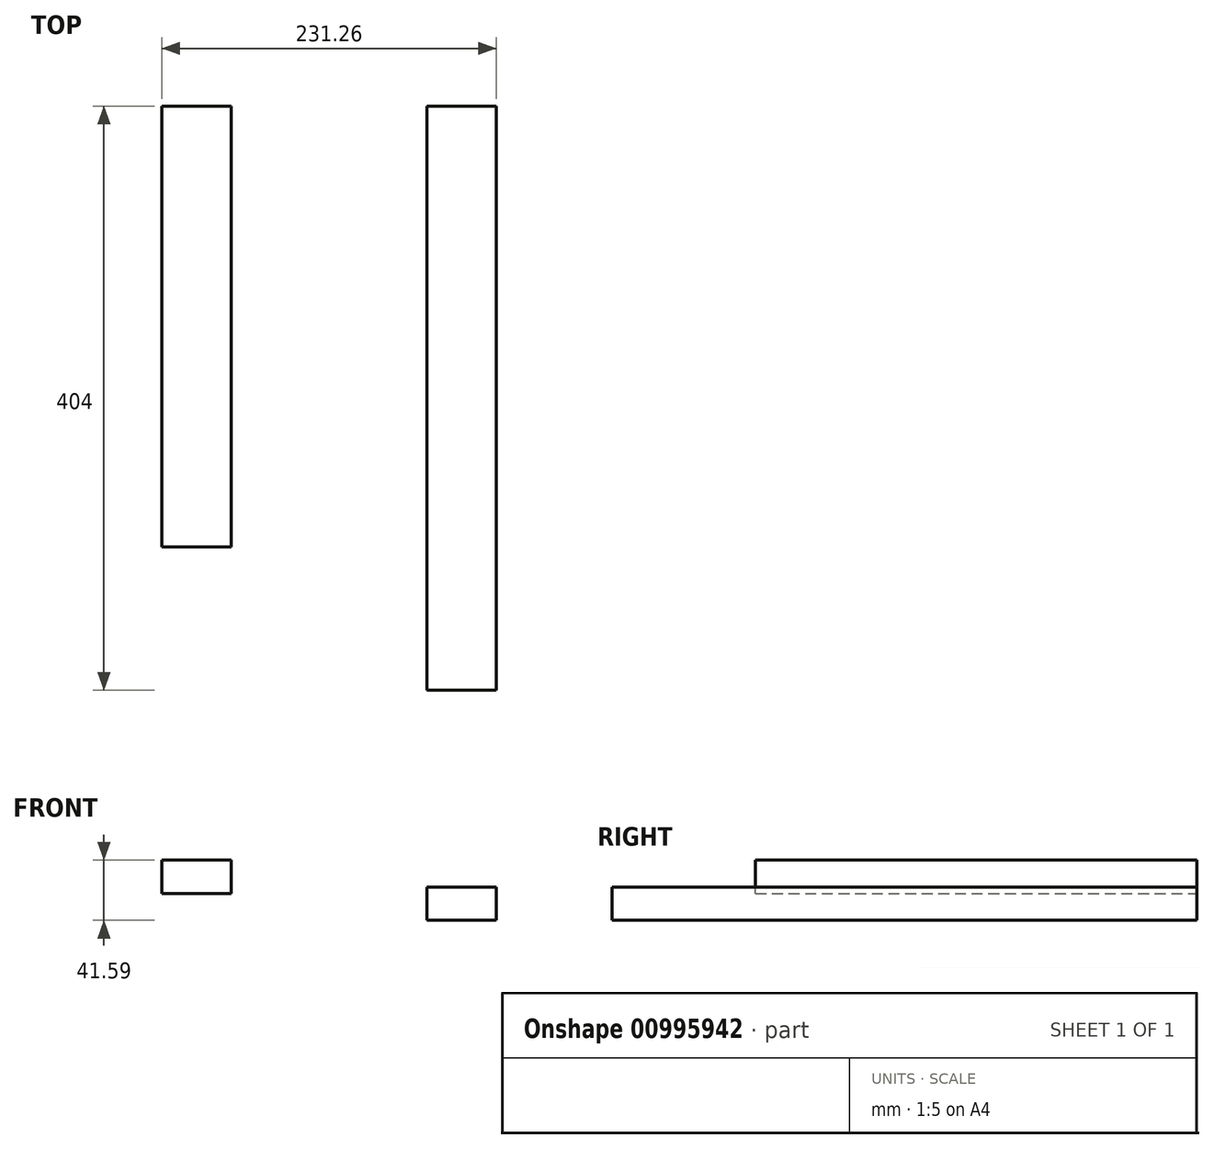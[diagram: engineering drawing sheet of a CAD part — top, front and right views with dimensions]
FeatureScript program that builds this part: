
annotation { "Feature Type Name" : "Feature", "Feature Type Description" : "" }
export const myFeature = defineFeature(function(context is Context, id is Id, definition is map)
    precondition{}
    {
        {
            assignVariable(context, id + "F0", {"name" : "Len", "anyValue" : 500 - 48 - 48});
        }
        {
            var Q0;
            Q0=qCreatedBy(makeId("Front.planeOp"),FACE);
            var sketch = newSketch(context, id + "F1", { "sketchPlane" : qUnion([Q0])});
            skLineSegment(sketch, "E0.bottom", {"start": v(24, 11.5) * mm, "end": v(-24, 11.5) * mm});
            skLineSegment(sketch, "E0.top", {"start": v(24, -11.5) * mm, "end": v(-24, -11.5) * mm});
            skLineSegment(sketch, "E0.left", {"start": v(24, 11.5) * mm, "end": v(24, -11.5) * mm});
            skLineSegment(sketch, "E0.right", {"start": v(-24, 11.5) * mm, "end": v(-24, -11.5) * mm});
            skPoint(sketch, "E0.middle", {"position": v(0, 0) * mm});
            skSolve(sketch);
        }
        {
            var Q0;
            Q0=qCreatedBy(makeId("Front.planeOp"),FACE);
            cPlane(context, id + "F2", {"entities" : qUnion([Q0]), "cplaneType" : CPlaneType.OFFSET, "offset" : (getVariable(context, 'Len')) * mm, "width" : 150 * mm, "height" : 150 * mm});
        }
        {
            var Q0;
            Q0=makeQuery(id+"F1.imprint","IMPRINT",FACE,{"disambiguationData":[TD([[makeQuery(id+"F1.imprint","IMPRINT",EDGE,{"derivedFrom":sQuery(id+"F1.wireOp",EDGE,"E0.bottom")}),1.0]])]});
            var Q1;
            Q1=qCreatedBy(id+"F2.planeOp",FACE);
            extrude(context, id + "F3", {"entities" : qUnion([Q0]), "endBound" : BoundingType.UP_TO_SURFACE, "depth" : 25 * mm, "endBoundEntityFace" : qUnion([Q1]), "offsetDistance" : 25 * mm});
        }
        {
            var Q0;
            Q0=qCreatedBy(makeId("Front.planeOp"),FACE);
            var sketch = newSketch(context, id + "F4", { "sketchPlane" : qUnion([Q0])});
            skLineSegment(sketch, "E1.bottom", {"start": v(-159.26, 7.09) * mm, "end": v(-207.26, 7.09) * mm});
            skLineSegment(sketch, "E1.top", {"start": v(-159.26, 30.09) * mm, "end": v(-207.26, 30.09) * mm});
            skLineSegment(sketch, "E1.left", {"start": v(-159.26, 7.09) * mm, "end": v(-159.26, 30.09) * mm});
            skLineSegment(sketch, "E1.right", {"start": v(-207.26, 7.09) * mm, "end": v(-207.26, 30.09) * mm});
            skPoint(sketch, "E1.middle", {"position": v(-183.26, 18.59) * mm});
            skSolve(sketch);
        }
        {
            assignVariable(context, id + "F5", {"name" : "Len2", "anyValue" : 305});
        }
        {
            var Q0;
            Q0=qCreatedBy(makeId("Front.planeOp"),FACE);
            cPlane(context, id + "F6", {"entities" : qUnion([Q0]), "cplaneType" : CPlaneType.OFFSET, "offset" : (getVariable(context, 'Len2')) * mm, "width" : 150 * mm, "height" : 150 * mm});
        }
        {
            var Q0;
            Q0=makeQuery(id+"F4.imprint","IMPRINT",FACE,{"disambiguationData":[TD([[makeQuery(id+"F4.imprint","IMPRINT",EDGE,{"derivedFrom":sQuery(id+"F4.wireOp",EDGE,"E1.bottom")}),-1.0]])]});
            var Q1;
            Q1=qCreatedBy(id+"F6.planeOp",FACE);
            extrude(context, id + "F7", {"entities" : qUnion([Q0]), "endBound" : BoundingType.UP_TO_SURFACE, "depth" : 25 * mm, "endBoundEntityFace" : qUnion([Q1]), "offsetDistance" : 25 * mm});
        }
    });
